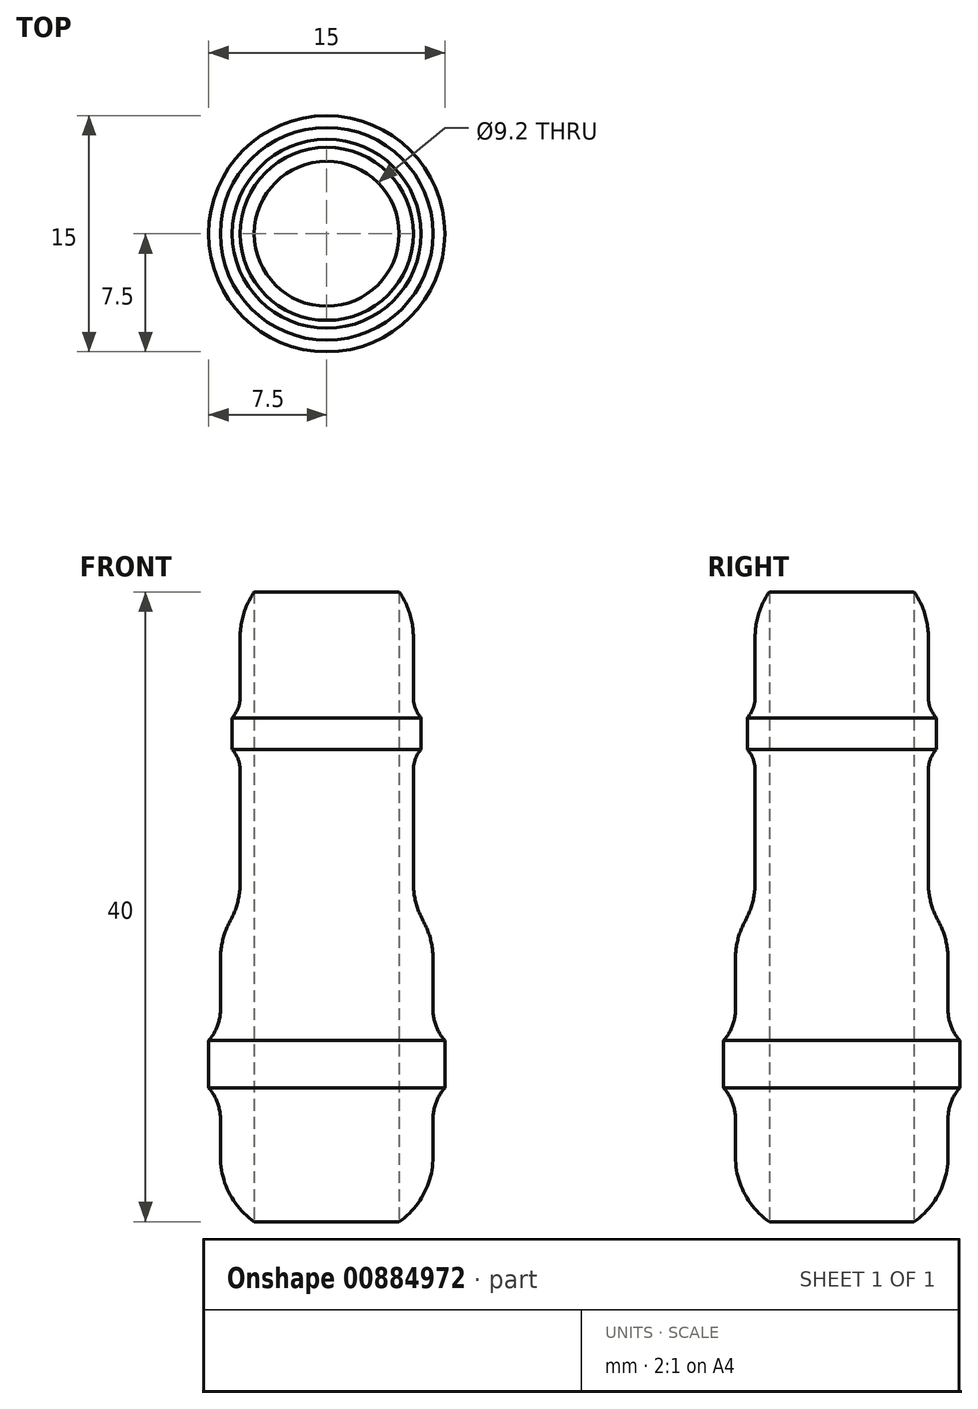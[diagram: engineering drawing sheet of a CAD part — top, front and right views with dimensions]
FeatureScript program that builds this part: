
annotation { "Feature Type Name" : "Feature", "Feature Type Description" : "" }
export const myFeature = defineFeature(function(context is Context, id is Id, definition is map)
    precondition{}
    {
        {
            var Q0;
            Q0=qCreatedBy(makeId("Top.planeOp"),FACE);
            var sketch = newSketch(context, id + "F0", { "sketchPlane" : qUnion([Q0])});
            skCircle(sketch, "E0", {"center": v(0, 0) * mm, "radius": 5.5 * mm});
            skCircle(sketch, "E1", {"center": v(0, 0) * mm, "radius": 4.6 * mm});
            skCircle(sketch, "E2", {"center": v(0, 0) * mm, "radius": 7.5 * mm});
            skCircle(sketch, "E3", {"center": v(0, 0) * mm, "radius": 6.75 * mm});
            skSolve(sketch);
        }
        {
            var Q0;
            Q0=makeQuery(id+"F0.imprint","IMPRINT",FACE,{"disambiguationData":[TD([[makeQuery(id+"F0.imprint","IMPRINT",EDGE,{"derivedFrom":sQuery(id+"F0.wireOp",EDGE,"E0")}),1.0]])]});
            extrude(context, id + "F1", {"entities" : qUnion([Q0]), "depth" : 20 * mm, "offsetDistance" : 25 * mm});
        }
        {
            var Q0;
            Q0=makeQuery(id+"F1.opExtrude","CAP_EDGE",EDGE,{"disambiguationData":[OSD([sQuery(id+"F0.wireOp",EDGE,"E0")])],"isStart":false});
            fillet(context, id + "F2", {"entities" : qUnion([Q0]), "radius" : 5 * mm, "tangentPropagation" : true, "allowEdgeOverflow" : false});
        }
        {
            var Q0;
            Q0=qCreatedBy(makeId("Top.planeOp"),FACE);
            cPlane(context, id + "F3", {"entities" : qUnion([Q0]), "cplaneType" : CPlaneType.OFFSET, "offset" : 10 * mm, "width" : 150 * mm, "height" : 150 * mm});
        }
        {
            var Q0;
            Q0=qCreatedBy(id+"F3.planeOp",FACE);
            var sketch = newSketch(context, id + "F4", { "sketchPlane" : qUnion([Q0])});
            skCircle(sketch, "E4", {"center": v(0, 0) * mm, "radius": 6 * mm});
            skSolve(sketch);
        }
        {
            var Q0;
            Q0=makeQuery(id+"F4.imprint","IMPRINT",FACE,{"disambiguationData":[TD([[makeQuery(id+"F4.imprint","IMPRINT",EDGE,{"derivedFrom":sQuery(id+"F4.wireOp",EDGE,"E4")}),1.0]])]});
            extrude(context, id + "F5", {"entities" : qUnion([Q0]), "operationType" : NewBodyOperationType.ADD, "depth" : 2 * mm, "offsetDistance" : 25 * mm});
        }
        {
            var Q0;
            {var subQ0=sQuery(id+"F0.wireOp",EDGE,"E0");Q0=makeQuery(id+"F5.boolean.opBoolean","INTERSECT",EDGE,{"derivedFrom":[makeQuery(id+"FVyywRFiOfjuPCi_1.boolean.opBoolean","SPLIT",FACE,{"disambiguationData":[TD([makeQuery(id+"F2.opFillet","BLEND_FACE",FACE,{"disambiguationData":[OSD([subQ0]),TDD([makeQuery(id+"F1.opExtrude","CAP_EDGE",EDGE,{"disambiguationData":[OSD([subQ0])],"isStart":false})])]})])],"derivedFrom":makeQuery(id+"F1.opExtrude","SWEPT_FACE",FACE,{"disambiguationData":[OSD([subQ0])]})}),makeQuery(id+"F5.opExtrude","CAP_FACE",FACE,{"disambiguationData":[OSD([sQuery(id+"F4.wireOp",EDGE,"E4")])],"isStart":false})]});}
            var Q1;
            {var subQ0=sQuery(id+"F0.wireOp",EDGE,"E0");Q1=makeQuery(id+"F5.boolean.opBoolean","INTERSECT",EDGE,{"derivedFrom":[makeQuery(id+"FVyywRFiOfjuPCi_1.boolean.opBoolean","SPLIT",FACE,{"disambiguationData":[TD([makeQuery(id+"F2.opFillet","BLEND_FACE",FACE,{"disambiguationData":[OSD([subQ0]),TDD([makeQuery(id+"F1.opExtrude","CAP_EDGE",EDGE,{"disambiguationData":[OSD([subQ0])],"isStart":false})])]})])],"derivedFrom":makeQuery(id+"F1.opExtrude","SWEPT_FACE",FACE,{"disambiguationData":[OSD([subQ0])]})}),makeQuery(id+"F5.opExtrude","CAP_FACE",FACE,{"disambiguationData":[OSD([sQuery(id+"F4.wireOp",EDGE,"E4")])],"isStart":true})]});}
            fillet(context, id + "F6", {"entities" : qUnion([Q0, Q1]), "radius" : 2 * mm, "tangentPropagation" : true, "allowEdgeOverflow" : false});
        }
        {
            var Q0;
            Q0=makeQuery(id+"F0.imprint","IMPRINT",FACE,{"disambiguationData":[TD([[makeQuery(id+"F0.imprint","IMPRINT",EDGE,{"derivedFrom":sQuery(id+"F0.wireOp",EDGE,"E1")}),1.0]])]});
            extrude(context, id + "F7", {"entities" : qUnion([Q0]), "operationType" : NewBodyOperationType.REMOVE, "oppositeDirection" : true, "depth" : 25 * mm, "offsetDistance" : 25 * mm, "hasSecondDirection" : true, "secondDirectionOppositeDirection" : false, "secondDirectionDepth" : 25 * mm});
        }
        {
            var Q0;
            Q0=makeQuery(id+"F0.imprint","IMPRINT",FACE,{"disambiguationData":[TD([[makeQuery(id+"F0.imprint","IMPRINT",EDGE,{"derivedFrom":sQuery(id+"F0.wireOp",EDGE,"E0")}),-1.0]])]});
            var Q1;
            Q1=makeQuery(id+"F0.imprint","IMPRINT",FACE,{"disambiguationData":[TD([[makeQuery(id+"F0.imprint","IMPRINT",EDGE,{"derivedFrom":sQuery(id+"F0.wireOp",EDGE,"E0")}),1.0]])]});
            extrude(context, id + "F8", {"entities" : qUnion([Q0, Q1]), "operationType" : NewBodyOperationType.ADD, "oppositeDirection" : true, "depth" : 20 * mm, "offsetDistance" : 25 * mm});
        }
        {
            var Q0;
            Q0=makeQuery(id+"F8.opExtrude","CAP_EDGE",EDGE,{"disambiguationData":[OSD([sQuery(id+"F0.wireOp",EDGE,"E3")])],"isStart":true});
            fillet(context, id + "F9", {"entities" : qUnion([Q0]), "radius" : 5 * mm, "tangentPropagation" : true, "allowEdgeOverflow" : false});
        }
        {
            var Q0;
            {var subQ0=sQuery(id+"F0.wireOp",EDGE,"E0");Q0=makeQuery(id+"F9.opFillet","BLEND_EDGE",EDGE,{"blendedFrom":[makeQuery(id+"F8.opExtrude","CAP_EDGE",EDGE,{"disambiguationData":[OSD([sQuery(id+"F0.wireOp",EDGE,"E3")])],"isStart":true}),makeQuery(id+"F5.boolean.opBoolean","SPLIT",FACE,{"disambiguationData":[TD([makeQuery(id+"F5.opExtrude","CAP_FACE",FACE,{"disambiguationData":[OSD([sQuery(id+"F4.wireOp",EDGE,"E4")])],"isStart":true})])],"derivedFrom":makeQuery(id+"F1.opExtrude","SWEPT_FACE",FACE,{"disambiguationData":[OSD([subQ0])]})})],"blendedInto":[makeQuery(id+"F5.boolean.opBoolean","SPLIT",FACE,{"disambiguationData":[TD([makeQuery(id+"F5.opExtrude","CAP_FACE",FACE,{"disambiguationData":[OSD([sQuery(id+"F4.wireOp",EDGE,"E4")])],"isStart":true})])],"derivedFrom":makeQuery(id+"F1.opExtrude","SWEPT_FACE",FACE,{"disambiguationData":[OSD([subQ0])]})})]});}
            fillet(context, id + "F10", {"entities" : qUnion([Q0]), "radius" : 5 * mm, "tangentPropagation" : true, "allowEdgeOverflow" : false});
        }
        {
            var Q0;
            Q0=makeQuery(id+"F8.opExtrude","CAP_EDGE",EDGE,{"disambiguationData":[OSD([sQuery(id+"F0.wireOp",EDGE,"E3")])],"isStart":false});
            fillet(context, id + "F11", {"entities" : qUnion([Q0]), "radius" : 5 * mm, "tangentPropagation" : true, "allowEdgeOverflow" : false});
        }
        {
            var Q0;
            Q0=qCreatedBy(makeId("Top.planeOp"),FACE);
            cPlane(context, id + "F12", {"entities" : qUnion([Q0]), "cplaneType" : CPlaneType.OFFSET, "offset" : 10 * mm, "oppositeDirection" : true, "width" : 150 * mm, "height" : 150 * mm});
        }
        {
            var Q0;
            Q0=qCreatedBy(id+"F12.planeOp",FACE);
            var sketch = newSketch(context, id + "F13", { "sketchPlane" : qUnion([Q0])});
            skCircle(sketch, "E5", {"center": v(0, 0) * mm, "radius": 7.5 * mm});
            skSolve(sketch);
        }
        {
            var Q0;
            Q0=makeQuery(id+"F13.imprint","IMPRINT",FACE,{"disambiguationData":[TD([[makeQuery(id+"F13.imprint","IMPRINT",EDGE,{"derivedFrom":sQuery(id+"F13.wireOp",EDGE,"E5")}),1.0]])]});
            extrude(context, id + "F14", {"entities" : qUnion([Q0]), "operationType" : NewBodyOperationType.ADD, "depth" : 1.5 * mm, "offsetDistance" : 25 * mm, "hasSecondDirection" : true, "secondDirectionOppositeDirection" : true, "secondDirectionDepth" : 1.5 * mm});
        }
        {
            var Q0;
            Q0=makeQuery(id+"F14.boolean.opBoolean","INTERSECT",EDGE,{"derivedFrom":[makeQuery(id+"F8.opExtrude","SWEPT_FACE",FACE,{"disambiguationData":[OSD([sQuery(id+"F0.wireOp",EDGE,"E3")])]}),makeQuery(id+"F14.opExtrude","CAP_FACE",FACE,{"disambiguationData":[OSD([sQuery(id+"F13.wireOp",EDGE,"E5")])],"isStart":true})]});
            var Q1;
            Q1=makeQuery(id+"F14.boolean.opBoolean","INTERSECT",EDGE,{"derivedFrom":[makeQuery(id+"F8.opExtrude","SWEPT_FACE",FACE,{"disambiguationData":[OSD([sQuery(id+"F0.wireOp",EDGE,"E3")])]}),makeQuery(id+"F14.opExtrude","CAP_FACE",FACE,{"disambiguationData":[OSD([sQuery(id+"F13.wireOp",EDGE,"E5")])],"isStart":false})]});
            fillet(context, id + "F15", {"entities" : qUnion([Q0, Q1]), "radius" : 3 * mm, "tangentPropagation" : true, "allowEdgeOverflow" : false});
        }
        {
            var Q0;
            {var subQ0=sQuery(id+"F0.wireOp",EDGE,"E1");Q0=makeQuery(id+"F14.boolean.opBoolean","SPLIT",FACE,{"disambiguationData":[TD([makeQuery(id+"F1.opExtrude","SWEPT_FACE",FACE,{"disambiguationData":[OSD([subQ0])]})])],"derivedFrom":makeQuery(id+"F14.opExtrude","CAP_FACE",FACE,{"disambiguationData":[OSD([sQuery(id+"F13.wireOp",EDGE,"E5")])],"isStart":true})});}
            extrude(context, id + "F16", {"entities" : qUnion([Q0]), "operationType" : NewBodyOperationType.REMOVE, "oppositeDirection" : true, "depth" : 25 * mm, "offsetDistance" : 25 * mm});
        }
    });
